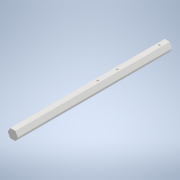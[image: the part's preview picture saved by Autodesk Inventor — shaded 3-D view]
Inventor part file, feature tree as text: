
AUTODESK INVENTOR PART (.ipt)
format: ipt  version: 2022 (Build 260153000, 153)  size: 121,344 bytes
history: native  units: mm
features: extrude x2, sketch x2
ambient origin geometry x8: Origin, YZ Plane, XZ Plane, XY Plane, X Axis, Y Axis, Z Axis, Center Point
bodies: Body1 (feature_tree)
feature tree (4):
  extrude  "Extrusion5"  Depth=3.1mm TaperAngle=360.0deg
  extrude  "Extrusion6"  Depth=95.0mm
  sketch  "Sketch7"  dims[d17=3.1mm d18=60.0mm d20=360.0deg]
  sketch  "Sketch8"  dims[d22=95.0mm d23=0.0mm d24=1.3mm d25=64.1mm d26=52.1mm d27=6.0mm d28=0.0mm d29=5.0mm d7=0.5mm d8=0.872665mm d9=0.5mm d10=0.872665mm]
